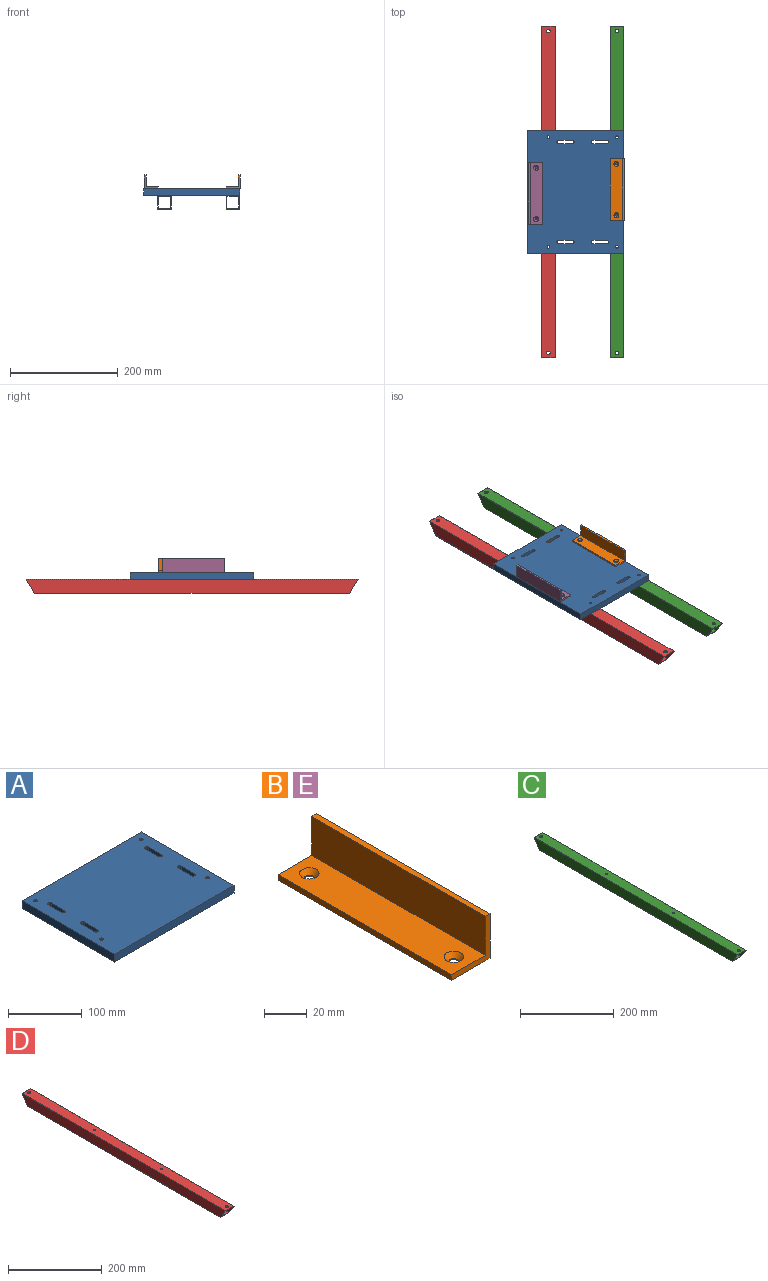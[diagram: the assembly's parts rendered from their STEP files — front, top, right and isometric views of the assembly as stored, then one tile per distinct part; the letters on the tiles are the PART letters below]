
ASSEMBLY  parts=5 mates=5
PART A: 26 faces, bbox 228.6x177.8x12.7 mm
  f0: plane 228.6x177.8mm, normal (0,0,1), area 39791.4mm2, adj f2,f3,f4,f5,f6,f7,f8,f9
  f1: plane 228.6x177.8mm, normal (0,0,-1), area 39791.4mm2, adj f2,f3,f4,f5,f6,f7,f8,f9
  f2: plane 177.8x12.7mm, normal (1,0,0), area 2258.1mm2, adj f0,f1,f3,f5
  f3: plane 228.6x12.7mm, normal (0,1,0), area 2903.2mm2, adj f0,f1,f2,f4
  f4: plane 177.8x12.7mm, normal (-1,0,0), area 2258.1mm2, adj f0,f1,f3,f5
  f5: plane 228.6x12.7mm, normal (0,-1,0), area 2903.2mm2, adj f0,f1,f2,f4
  f6: cylinder r=2.55mm len=12.7mm, axis (0,0,1), area 203.7mm2, adj f0,f1
  f7: cylinder r=2.55mm len=12.7mm, axis (0,0,1), area 203.7mm2, adj f0,f1
  f8: cylinder r=2.55mm len=12.7mm, axis (0,0,1), area 203.7mm2, adj f0,f1
  f9: cylinder r=2.55mm len=12.7mm, axis (0,0,1), area 203.7mm2, adj f0,f1
  f10: cylinder r=3.17mm len=12.7mm, axis (0,0,1), area 126.7mm2, adj f0,f1,f11,f13
  f11: plane 25.4x12.7mm, normal (1,0,0), area 322.6mm2, adj f0,f1,f10,f12
  f12: cylinder r=3.17mm len=12.7mm, axis (0,0,1), area 126.7mm2, adj f0,f1,f11,f13
  f13: plane 25.4x12.7mm, normal (-1,0,0), area 322.6mm2, adj f0,f1,f10,f12
  f14: plane 25.4x12.7mm, normal (1,0,0), area 322.6mm2, adj f0,f1,f15,f17
  f15: cylinder r=3.17mm len=12.7mm, axis (0,0,1), area 126.7mm2, adj f0,f1,f14,f16
  f16: plane 25.4x12.7mm, normal (-1,0,0), area 322.6mm2, adj f0,f1,f15,f17
  f17: cylinder r=3.17mm len=12.7mm, axis (0,0,1), area 126.7mm2, adj f0,f1,f14,f16
  f18: cylinder r=3.17mm len=12.7mm, axis (0,0,1), area 126.7mm2, adj f0,f1,f19,f21
  f19: plane 25.4x12.7mm, normal (1,0,0), area 322.6mm2, adj f0,f1,f18,f20
  f20: cylinder r=3.17mm len=12.7mm, axis (0,0,1), area 126.7mm2, adj f0,f1,f19,f21
  f21: plane 25.4x12.7mm, normal (-1,0,0), area 322.6mm2, adj f0,f1,f18,f20
  f22: cylinder r=3.17mm len=12.7mm, axis (0,0,1), area 126.7mm2, adj f0,f1,f23,f25
  f23: plane 25.4x12.7mm, normal (1,0,0), area 322.6mm2, adj f0,f1,f22,f24
  f24: cylinder r=3.17mm len=12.7mm, axis (0,0,1), area 126.7mm2, adj f0,f1,f23,f25
  f25: plane 25.4x12.7mm, normal (-1,0,0), area 322.6mm2, adj f0,f1,f22,f24
PART B: 12 faces, bbox 25.4x114.3x25.4 mm
  f0: plane 114.3x22.23mm, normal (-1,0,0), area 2540.3mm2, adj f1,f5,f6,f7
  f1: plane 114.3x22.23mm, normal (0,0,1), area 2409.7mm2, adj f0,f2,f6,f7,f9,f11
  f2: plane 114.3x3.18mm, normal (-1,0,0), area 362.9mm2, adj f1,f3,f6,f7
  f3: plane 114.3x25.4mm, normal (0,0,-1), area 2871.5mm2, adj f2,f4,f6,f7,f8,f10
  f4: plane 114.3x25.4mm, normal (1,0,0), area 2903.2mm2, adj f3,f5,f6,f7
  f5: plane 114.3x3.18mm, normal (0,0,1), area 362.9mm2, adj f0,f4,f6,f7
  f6: plane 25.4x25.4mm, normal (0,-1,0), area 151.2mm2, adj f0,f1,f2,f3,f4,f5
  f7: plane 25.4x25.4mm, normal (0,1,0), area 151.2mm2, adj f0,f1,f2,f3,f4,f5
  f8: cylinder r=2.25mm len=4.5mm, axis (0,0,1), area 7.3mm2, adj f3,f9
  f9: cone r=2.25mm half-angle=41deg, axis (0,0,1), area 75.3mm2, adj f1,f8
  f10: cylinder r=2.25mm len=4.5mm, axis (0,0,1), area 7.3mm2, adj f3,f11
  f11: cone r=2.25mm half-angle=41deg, axis (0,0,1), area 75.3mm2, adj f1,f10
PART C: 16 faces, bbox 25.4x616x25.4 mm
  f0: plane 615.95x25.4mm, normal (1,0,0), area 15241.9mm2, adj f1,f7,f10,f11
  f1: plane 584.2x25.4mm, normal (0,0,-1), area 14585.3mm2, adj f0,f2,f10,f11,f12,f13
  f2: plane 615.95x25.4mm, normal (-1,0,0), area 15241.9mm2, adj f1,f7,f10,f11
  f3: plane 613.97x22.23mm, normal (0,0,-1), area 13532.7mm2, adj f4,f6,f8,f9,f10,f11,f14,f15
  f4: plane 613.97x22.23mm, normal (1,0,0), area 13336.7mm2, adj f3,f5,f10,f11
  f5: plane 586.18x22.23mm, normal (0,0,1), area 12774.6mm2, adj f4,f6,f10,f11,f12,f13
  f6: plane 613.97x22.23mm, normal (-1,0,0), area 13336.7mm2, adj f3,f5,f10,f11
  f7: plane 615.95x25.4mm, normal (0,0,1), area 15532.5mm2, adj f0,f2,f8,f9,f10,f11,f14,f15
  f8: cylinder r=2.55mm len=5.11mm, axis (0,0,1), area 25.5mm2, adj f3,f7
  f9: cylinder r=2.55mm len=5.11mm, axis (0,0,1), area 25.5mm2, adj f3,f7
  f10: plane 25.4x25.4mm, normal (0,-0.85,-0.53), area 178.3mm2, adj f0,f1,f2,f3,f4,f5,f6,f7
  f11: plane 25.4x25.4mm, normal (0,0.85,-0.53), area 178.3mm2, adj f0,f1,f2,f3,f4,f5,f6,f7
  f12: cylinder r=6.35mm len=12.7mm, axis (0,0,-1), area 63.3mm2, adj f1,f5
  f13: cylinder r=6.35mm len=12.7mm, axis (0,0,-1), area 63.3mm2, adj f1,f5
  f14: cylinder r=3.38mm len=6.76mm, axis (0,0,1), area 33.7mm2, adj f3,f7
  f15: cylinder r=3.38mm len=6.76mm, axis (0,0,1), area 33.7mm2, adj f3,f7
PART D: 16 faces, bbox 25.4x616x25.4 mm
  f0: plane 615.95x25.4mm, normal (-1,0,0), area 15241.9mm2, adj f1,f7,f10,f11
  f1: plane 584.2x25.4mm, normal (0,0,-1), area 14585.3mm2, adj f0,f2,f10,f11,f12,f13
  f2: plane 615.95x25.4mm, normal (1,0,0), area 15241.9mm2, adj f1,f7,f10,f11
  f3: plane 613.97x22.23mm, normal (0,0,-1), area 13532.7mm2, adj f4,f6,f8,f9,f10,f11,f14,f15
  f4: plane 613.97x22.23mm, normal (-1,0,0), area 13336.7mm2, adj f3,f5,f10,f11
  f5: plane 586.18x22.23mm, normal (0,0,1), area 12774.6mm2, adj f4,f6,f10,f11,f12,f13
  f6: plane 613.97x22.23mm, normal (1,0,0), area 13336.7mm2, adj f3,f5,f10,f11
  f7: plane 615.95x25.4mm, normal (0,0,1), area 15532.5mm2, adj f0,f2,f8,f9,f10,f11,f14,f15
  f8: cylinder r=2.55mm len=5.11mm, axis (0,0,1), area 25.5mm2, adj f3,f7
  f9: cylinder r=2.55mm len=5.11mm, axis (0,0,1), area 25.5mm2, adj f3,f7
  f10: plane 25.4x25.4mm, normal (0,-0.85,-0.53), area 178.3mm2, adj f0,f1,f2,f3,f4,f5,f6,f7
  f11: plane 25.4x25.4mm, normal (0,0.85,-0.53), area 178.3mm2, adj f0,f1,f2,f3,f4,f5,f6,f7
  f12: cylinder r=6.35mm len=12.7mm, axis (0,0,-1), area 63.3mm2, adj f1,f5
  f13: cylinder r=6.35mm len=12.7mm, axis (0,0,-1), area 63.3mm2, adj f1,f5
  f14: cylinder r=3.38mm len=6.76mm, axis (0,0,1), area 33.7mm2, adj f3,f7
  f15: cylinder r=3.38mm len=6.76mm, axis (0,0,1), area 33.7mm2, adj f3,f7
PART E: same geometry as B
PLACE A rot(axis=(0,0,-1),90deg) t=(-23.92,-419.41,-30.11)mm
PLACE B t=(67.33,-243.43,-17.41)mm
PLACE C rot(axis=(0,0,1),180deg) t=(64.98,-613.08,-55.51)mm
PLACE D rot(axis=(0,0,1),180deg) t=(90.38,-613.08,-55.51)mm
PLACE E rot(axis=(0,0,1),180deg) t=(64.35,-364.96,-17.41)mm
MATE fastened A.f6 <-> D.f13  axis (0,0,-1) through (14.18,-406.71,-30.11)mm
MATE planar E.f3 <-> A.f0  axis (0,0,-1) through (-10.28,-307.81,-17.41)mm
MATE fastened A.f7 <-> C.f13  axis (0,0,-1) through (141.18,-406.71,-30.11)mm
MATE planar A.f0 <-> B.f3  axis (0,0,1) through (64.7,-305.11,-17.41)mm
MATE parallel E.f0 <-> B.f0  axis (1,0,0) through (-19.78,-307.81,-3.12)mm
